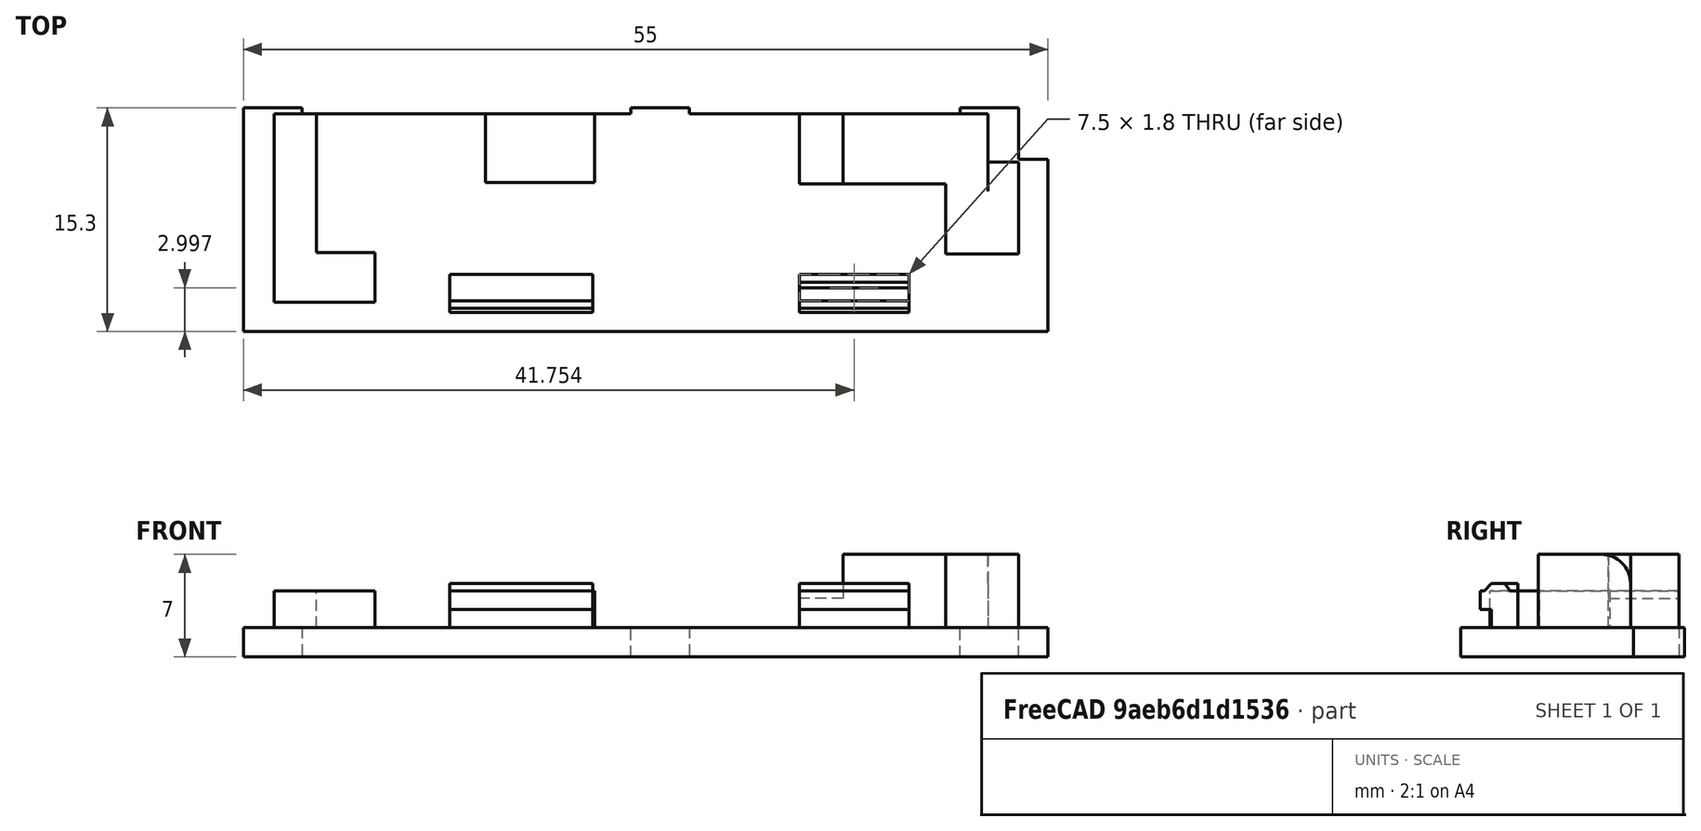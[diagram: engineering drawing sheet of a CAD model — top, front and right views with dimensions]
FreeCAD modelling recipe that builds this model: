
FCSTD DOCUMENT  (FreeCAD 0.18.4R)
Label: lamp.base.ps.cup
License: All rights reserved
LicenseURL: http://en.wikipedia.org/wiki/All_rights_reserved
objects: Part::Extrusion×15, Part::Feature×13, Part::MultiFuse×7, Part::Cut×6, Part::Part2DObjectPython×5
note: 46 computed .brp shape members not serialized (recipe doc carries the construction recipe); baked Part::Feature solids carry a one-line shape summary decoded from their .brp

FEATURE [Part::Feature] Fusion076089004005008002002002002003004002009002004002005004002003004001  label="lamp.base.ps.cup"
  Placement = pos=(0,-650.213,-632.212) rot=(-1,0,0;1.5708rad)
  shape: bbox 53 x 15.1 x 7 mm, 47 faces (baked)
FEATURE [Part::Feature] Face
  Placement = pos=(0,-650.213,-632.212) rot=(-1,0,0;1.5708rad)
  shape: bbox 10 x 6.04e-07 x 1.25 mm, 1 faces, 0 solids (baked)
FEATURE [Part::Extrusion] Extrusion
  Base = -> Face
  Dir = (9e-16,-0.278642,1.09e-14)
  DirMode = 0
  FaceMakerClass = Part::FaceMakerBullseye
  LengthFwd = 0
  LengthRev = 0
  Solid = true
  Symmetric = false
FEATURE [Part::Feature] Face001
  Placement = pos=(0,-650.213,-632.212) rot=(-1,0,0;1.5708rad)
  shape: bbox 6.04e-07 x 2.3 x 3 mm, 1 faces, 0 solids (baked)
FEATURE [Part::Extrusion] Extrusion001
  Base = -> Face001
  Dir = (0.1,3e-16,0)
  DirMode = 0
  FaceMakerClass = Part::FaceMakerBullseye
  LengthFwd = 0
  LengthRev = 0
  Solid = true
  Symmetric = false
FEATURE [Part::Cut] Cut
  Base = -> Fusion076089004005008002002002002003004002009002004002005004002003004001
  Tool = -> Extrusion001
FEATURE [Part::Feature] Face002
  shape: bbox 6.04e-07 x 0.2786 x 1.25 mm, 1 faces, 0 solids (baked)
FEATURE [Part::Extrusion] Extrusion002
  Base = -> Face002
  Dir = (0.1,3e-16,-3e-16)
  DirMode = 0
  FaceMakerClass = Part::FaceMakerBullseye
  LengthFwd = 0
  LengthRev = 0
  Solid = true
  Symmetric = false
FEATURE [Part::Cut] Cut001
  Base = -> Extrusion
  Tool = -> Extrusion002
FEATURE [Part::Feature] Face003
  Placement = pos=(0,-650.213,-632.212) rot=(-1,0,0;1.5708rad)
  shape: bbox 6.04e-07 x 2.3 x 3 mm, 1 faces, 0 solids (baked)
FEATURE [Part::Extrusion] Extrusion003
  Base = -> Face003
  Dir = (-0.1,0,0)
  DirMode = 0
  FaceMakerClass = Part::FaceMakerBullseye
  LengthFwd = 0
  LengthRev = 0
  Solid = true
  Symmetric = false
FEATURE [Part::Feature] Face004
  shape: bbox 6.04e-07 x 0.2786 x 1.25 mm, 1 faces, 0 solids (baked)
FEATURE [Part::Extrusion] Extrusion004
  Base = -> Face004
  Dir = (-0.1,-3e-16,3e-16)
  DirMode = 0
  FaceMakerClass = Part::FaceMakerBullseye
  LengthFwd = 0
  LengthRev = 0
  Solid = true
  Symmetric = false
FEATURE [Part::Cut] Cut002
  Base = -> Cut
  Tool = -> Extrusion003
FEATURE [Part::Cut] Cut003
  Base = -> Cut001
  Tool = -> Extrusion004
FEATURE [Part::MultiFuse] Fusion
  Shapes = -> [Cut003,Cut002]
FEATURE [Part::Feature] Face005
  Placement = pos=(69.5036,-626.113,9.00025) rot=(-1,0,0;1.5708rad)
  shape: bbox 4 x 6.04e-07 x 2 mm, 1 faces, 0 solids (baked)
FEATURE [Part::Extrusion] Extrusion005
  Base = -> Face005
  Dir = (1e-16,0.1,-1.7e-15)
  DirMode = 0
  FaceMakerClass = Part::FaceMakerBullseye
  LengthFwd = 0
  LengthRev = 0
  Solid = true
  Symmetric = false
FEATURE [Part::Feature] Face006
  Placement = pos=(43.0036,-626.113,9.00025) rot=(-1,0,0;1.5708rad)
  shape: bbox 4 x 6.04e-07 x 2 mm, 1 faces, 0 solids (baked)
FEATURE [Part::Extrusion] Extrusion006
  Base = -> Face006
  Dir = (1e-16,0.1,-1.7e-15)
  DirMode = 0
  FaceMakerClass = Part::FaceMakerBullseye
  LengthFwd = 0
  LengthRev = 0
  Solid = true
  Symmetric = false
FEATURE [Part::Feature] Face007
  Placement = pos=(92.0036,-626.113,9.00025) rot=(-1,0,0;1.5708rad)
  shape: bbox 4 x 6.04e-07 x 2 mm, 1 faces, 0 solids (baked)
FEATURE [Part::Extrusion] Extrusion007
  Base = -> Face007
  Dir = (1e-16,0.1,-1.7e-15)
  DirMode = 0
  FaceMakerClass = Part::FaceMakerBullseye
  LengthFwd = 0
  LengthRev = 0
  Solid = true
  Symmetric = false
FEATURE [Part::MultiFuse] Fusion076089004005008002002002002003004002009002004002005004002003004002  label="LAMP.BASE.PS.CUP"
  Shapes = -> [Extrusion006,Extrusion005,Extrusion007,Fusion]
FEATURE [Part::Feature] Face008
  Placement = pos=(43.0036,-626.013,9.00025) rot=(-1,0,0;1.5708rad)
  shape: bbox 4 x 6.04e-07 x 2 mm, 1 faces, 0 solids (baked)
FEATURE [Part::Extrusion] Extrusion008
  Base = -> Face008
  Dir = (1e-16,0.1,-1.7e-15)
  DirMode = 0
  FaceMakerClass = Part::FaceMakerBullseye
  LengthFwd = 0
  LengthRev = 0
  Solid = true
  Symmetric = false
FEATURE [Part::Feature] Face009
  Placement = pos=(69.5036,-626.013,9.00025) rot=(-1,0,0;1.5708rad)
  shape: bbox 4 x 6.04e-07 x 2 mm, 1 faces, 0 solids (baked)
FEATURE [Part::Extrusion] Extrusion009
  Base = -> Face009
  Dir = (1e-16,0.1,-1.7e-15)
  DirMode = 0
  FaceMakerClass = Part::FaceMakerBullseye
  LengthFwd = 0
  LengthRev = 0
  Solid = true
  Symmetric = false
FEATURE [Part::Feature] Face010
  Placement = pos=(92.0036,-626.013,9.00025) rot=(-1,0,0;1.5708rad)
  shape: bbox 4 x 6.04e-07 x 2 mm, 1 faces, 0 solids (baked)
FEATURE [Part::Extrusion] Extrusion010
  Base = -> Face010
  Dir = (1e-16,0.1,-1.7e-15)
  DirMode = 0
  FaceMakerClass = Part::FaceMakerBullseye
  LengthFwd = 0
  LengthRev = 0
  Solid = true
  Symmetric = false
FEATURE [Part::MultiFuse] Fusion076089004005008002002002002003004002009002004002005004002003004003
  Shapes = -> [Extrusion010,Extrusion009,Extrusion008]
FEATURE [Part::MultiFuse] Fusion076089004005008002002002002003004002009002004002005004002003004004  label="LAMP.BASE.PS.CUP001"
  Shapes = -> [Fusion076089004005008002002002002003004002009002004002005004002003004003,Fusion076089004005008002002002002003004002009002004002005004002003004002]
FEATURE [Part::Part2DObjectPython] Wire001  # Draft 2D object (typed FeaturePython)
  ChamferSize = 0
  Closed = true
  End = (81.0036,-638.213,12.0003)
  FilletRadius = 0
  Length = 8.29648
  MakeFace = true
  Placement = pos=(81.0036,-639.113,9.00025) rot=(0.57735,-0.57735,-0.57735;2.0944rad)
  Points = (7) [(0,0,0),(0,1.25,7.10543e-15),(0.778642,1.25,1.42109e-14),(0.778642,2.5,7.10543e-15),(0.5,2.5,0),(-5.68434e-13,3,0),(-0.9,3,0)]
  Start = (81.0036,-639.113,9.00025)
  Subdivisions = 0
  Support = -> [Fusion076089004005008002002002002003004002009002004002005004002003004004]
FEATURE [Part::Extrusion] Extrusion012
  Base = -> Wire001
  Dir = (7.5,-4.56e-14,4.2e-15)
  DirMode = 0
  FaceMakerClass = Part::FaceMakerBullseye
  LengthFwd = 0
  LengthRev = 0
  Solid = true
  Symmetric = false
FEATURE [Part::MultiFuse] Fusion076089004005008002002002002003004002009002004002005004002003004005
  Shapes = -> [Extrusion012,Fusion076089004005008002002002002003004002009002004002005004002003004004]
FEATURE [Part::Part2DObjectPython] Wire  # Draft 2D object (typed FeaturePython)
  ChamferSize = 0
  Closed = true
  End = (81.0036,-638.363,11.5003)
  FilletRadius = 0
  Length = 1.67202
  MakeFace = true
  Placement = pos=(81.0036,-638.213,12.0003) rot=(0.57735,-0.57735,-0.57735;2.0944rad)
  Points = (3) [(0,0,0),(-0.375,-0.5,0),(0.15,-0.5,0)]
  Start = (81.0036,-638.213,12.0003)
  Subdivisions = 0
  Support = -> [Fusion076089004005008002002002002003004002009002004002005004002003004005]
FEATURE [Part::Extrusion] Extrusion013
  Base = -> Wire
  Dir = (7.5,0,0)
  DirMode = 0
  FaceMakerClass = Part::FaceMakerBullseye
  LengthFwd = 0
  LengthRev = 0
  Solid = true
  Symmetric = false
FEATURE [Part::MultiFuse] Fusion076089004005008002002002002003004002009002004002005004002003004006  label="LAMP.BASE.PS.CUP002"
  Shapes = -> [Fusion076089004005008002002002002003004002009002004002005004002003004005,Extrusion013]
FEATURE [Part::Part2DObjectPython] Rectangle  # Draft 2D object (typed FeaturePython)
  ChamferSize = 0
  Columns = 1
  FilletRadius = 0
  Height = 2
  Length = 11.8
  MakeFace = true
  Placement = pos=(96.0036,-641.213,7.00025) rot=(0.57735,0.57735,0.57735;2.0944rad)
  Rows = 1
FEATURE [Part::Extrusion] Extrusion014
  Base = -> Rectangle
  Dir = (2,0,0)
  DirMode = 0
  FaceMakerClass = Part::FaceMakerBullseye
  LengthFwd = 0
  LengthRev = 0
  Solid = true
  Symmetric = false
FEATURE [Part::MultiFuse] Fusion076089004005008002002002002003004002009002004002005004002003004007
  Shapes = -> [Fusion076089004005008002002002002003004002009002004002005004002003004006,Extrusion014]
FEATURE [Part::Feature] Fusion076089004005008002002002002003004002009002004002005004002003004007001  label="lamp.base.ps.cup001"
  shape: bbox 55 x 15.3 x 7 mm, 56 faces (baked)
FEATURE [Part::Part2DObjectPython] Rectangle001  # Draft 2D object (typed FeaturePython)
  ChamferSize = 0
  Columns = 1
  FilletRadius = 0
  Height = 2
  Length = 2
  MakeFace = true
  Placement = pos=(96.0036,-631.613,12.0003) rot=(0.57735,0.57735,0.57735;2.0944rad)
  Rows = 1
  Support = -> [Fusion076089004005008002002002002003004002009002004002005004002003004007001]
FEATURE [Part::Part2DObjectPython] Circle  # Draft 2D object (typed FeaturePython)
  FirstAngle = 0
  LastAngle = 0
  MakeFace = true
  Placement = pos=(96.0036,-631.613,12.0003) rot=(0.57735,0.57735,0.57735;2.0944rad)
  Radius = 2
FEATURE [Part::Cut] Cut004
  Base = -> Rectangle001
  Tool = -> Circle
FEATURE [Part::Extrusion] Extrusion015
  Base = -> Cut004
  Dir = (-2.1,4.76e-14,-4.76e-14)
  DirMode = 0
  FaceMakerClass = Part::FaceMakerBullseye
  LengthFwd = 0
  LengthRev = 0
  Solid = true
  Symmetric = false
FEATURE [Part::Cut] Cut005  label="lamp.base.ps.cup002"
  Base = -> Fusion076089004005008002002002002003004002009002004002005004002003004007001
  Tool = -> Extrusion015
